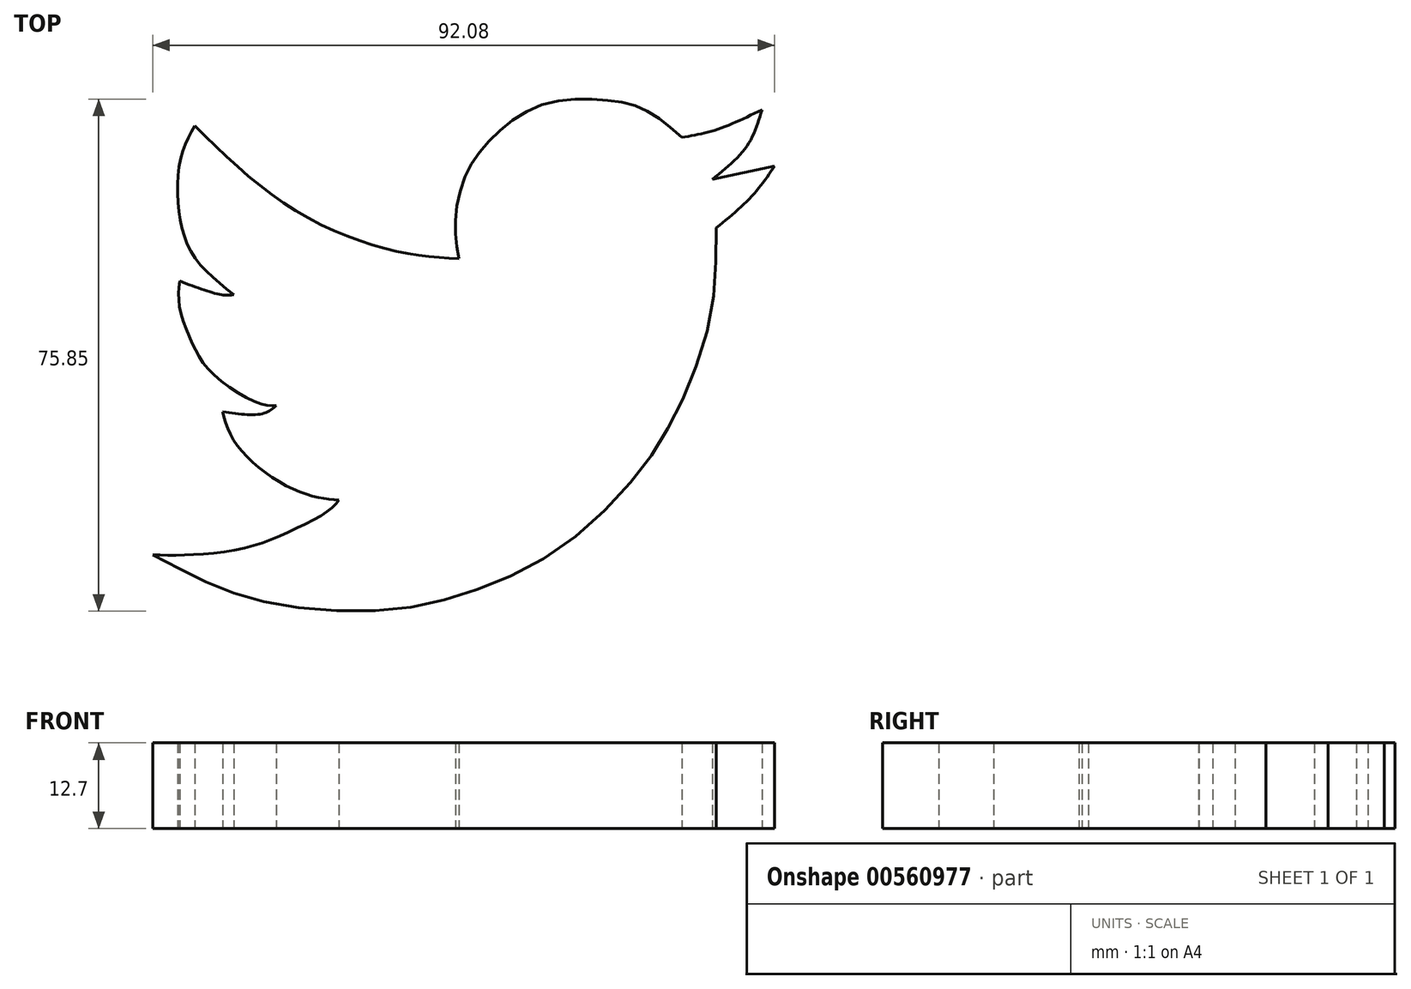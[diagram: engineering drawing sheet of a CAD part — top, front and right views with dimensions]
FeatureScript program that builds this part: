
annotation { "Feature Type Name" : "Feature", "Feature Type Description" : "" }
export const myFeature = defineFeature(function(context is Context, id is Id, definition is map)
    precondition{}
    {
        {
            var Q0;
            Q0=qCreatedBy(makeId("Top.planeOp"),FACE);
            var sketch = newSketch(context, id + "F0", { "sketchPlane" : qUnion([Q0])});
            skFitSpline(sketch, "E0", {"points": [v(-41.7, 10.34) * mm, v(-43.77, 5.46) * mm, v(-43.99, -2.5) * mm, v(-41.7, -9.17) * mm, v(-35.88, -14.69) * mm], "startDerivative": vector(-11.25, -20.54) * mm, "endDerivative": vector(24.7, -19.44) * mm});
            skFitSpline(sketch, "E1", {"points": [v(-35.88, -14.69) * mm, v(-37.75, -14.69) * mm, v(-43.91, -12.68) * mm], "startDerivative": vector(-4.62, -0.54) * mm, "endDerivative": vector(-10.82, 4.09) * mm});
            skFitSpline(sketch, "E2", {"points": [v(-43.91, -12.68) * mm, v(-43.91, -16.55) * mm, v(-42.05, -21.86) * mm, v(-39.04, -26.38) * mm, v(-32.15, -30.75) * mm, v(-29.57, -31.1) * mm], "startDerivative": vector(-2.02, -20.96) * mm, "endDerivative": vector(15.34, 0.23) * mm});
            skFitSpline(sketch, "E3", {"points": [v(-29.57, -31.1) * mm, v(-31.72, -32.33) * mm, v(-37.53, -32.04) * mm], "startDerivative": vector(-4.63, -3.8) * mm, "endDerivative": vector(-10.85, 1.55) * mm});
            skFitSpline(sketch, "E4", {"points": [v(-37.53, -32.04) * mm, v(-36.38, -35.46) * mm, v(-32.97, -39.63) * mm, v(-27.34, -43.39) * mm, v(-23.08, -44.8) * mm, v(-20.3, -45.13) * mm], "startDerivative": vector(4.7, -18.98) * mm, "endDerivative": vector(16.88, -1.43) * mm});
            skFitSpline(sketch, "E5", {"points": [v(-20.3, -45.13) * mm, v(-22.14, -46.88) * mm, v(-27.68, -49.78) * mm, v(-34.37, -52.25) * mm, v(-42.69, -53.24) * mm, v(-47.89, -53.24) * mm], "startDerivative": vector(-11.17, -12.89) * mm, "endDerivative": vector(-25.24, 0.56) * mm});
            skFitSpline(sketch, "E6", {"points": [v(-47.89, -53.24) * mm, v(-39.15, -57.58) * mm, v(-28.83, -60.7) * mm, v(-13.18, -61.38) * mm, v(-0.6, -58.65) * mm, v(12.84, -51.94) * mm, v(24.23, -40.78) * mm, v(30.14, -31.1) * mm, v(34.72, -17.7) * mm, v(35.57, -4.79) * mm], "startDerivative": vector(90.08, -47.9) * mm, "endDerivative": vector(-0.03, 115.27) * mm});
            skFitSpline(sketch, "E7", {"points": [v(35.57, -4.79) * mm, v(40.93, 0) * mm, v(44.2, 4.38) * mm], "startDerivative": vector(10.85, 8.84) * mm, "endDerivative": vector(6.28, 9.5) * mm});
            skFitSpline(sketch, "E8", {"points": [v(44.2, 4.38) * mm, v(34.96, 2.39) * mm], "startDerivative": vector(-9.23, -1.99) * mm, "endDerivative": vector(-9.23, -1.99) * mm});
            skFitSpline(sketch, "E9", {"points": [v(34.96, 2.39) * mm, v(40.15, 7.4) * mm, v(42.32, 12.7) * mm], "startDerivative": vector(11.19, 9) * mm, "endDerivative": vector(3.38, 11.68) * mm});
            skFitSpline(sketch, "E10", {"points": [v(42.32, 12.7) * mm, v(35.57, 9.74) * mm, v(30.44, 8.6) * mm], "startDerivative": vector(-12.8, -6.25) * mm, "endDerivative": vector(-10.9, -1.83) * mm});
            skFitSpline(sketch, "E11", {"points": [v(30.44, 8.6) * mm, v(24.96, 12.7) * mm, v(18.8, 14.15) * mm, v(9.7, 13.42) * mm, v(2.46, 8.6) * mm, v(-1.51, 3.05) * mm, v(-3.08, -4) * mm, v(-2.54, -9.37) * mm], "startDerivative": vector(-38.3, 33.8) * mm, "endDerivative": vector(7.25, -41.22) * mm});
            skFitSpline(sketch, "E12", {"points": [v(-2.54, -9.37) * mm, v(-12.19, -8.16) * mm, v(-27.32, -1.9) * mm, v(-41.7, 10.34) * mm], "startDerivative": vector(-33.6, 2.15) * mm, "endDerivative": vector(-36.11, 35.4) * mm});
            skSolve(sketch);
        }
        {
            var Q0;
            Q0=makeQuery(id+"F0.imprint","IMPRINT",FACE,{"disambiguationData":[TD([[makeQuery(id+"F0.imprint","IMPRINT",EDGE,{"derivedFrom":sQuery(id+"F0.wireOp",EDGE,"E0")}),1.0]])]});
            extrude(context, id + "F1", {"entities" : qUnion([Q0]), "depth" : 12.7 * mm, "offsetDistance" : 25.4 * mm});
        }
    });
